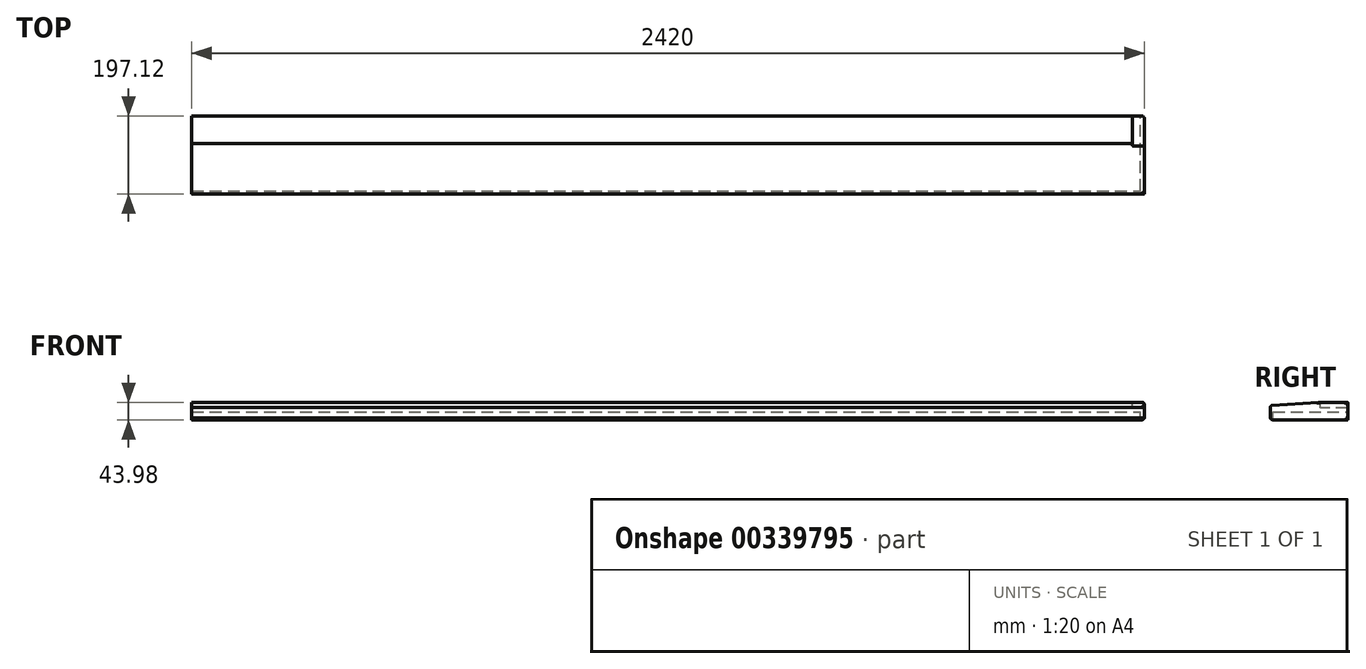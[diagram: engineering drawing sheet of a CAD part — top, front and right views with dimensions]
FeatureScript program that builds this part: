
annotation { "Feature Type Name" : "Feature", "Feature Type Description" : "" }
export const myFeature = defineFeature(function(context is Context, id is Id, definition is map)
    precondition{}
    {
        {
            var Q0;
            Q0=qCreatedBy(makeId("Right.planeOp"),FACE);
            var sketch = newSketch(context, id + "F0", { "sketchPlane" : qUnion([Q0])});
            skLineSegment(sketch, "E0", {"start": v(0, 0) * mm, "end": v(190, 0) * mm});
            skLineSegment(sketch, "E1", {"start": v(-7.12, 10.81) * mm, "end": v(-6.34, -15.77) * mm});
            skLineSegment(sketch, "E2", {"start": v(-1.62, -19.82) * mm, "end": v(0, -19.82) * mm});
            skLineSegment(sketch, "E3", {"start": v(0, -19.82) * mm, "end": v(0, 0) * mm});
            skPoint(sketch, "E4.visualSharp", {"position": v(-8.9, -5.66) * mm});
            skArc(sketch, "E4.filletArc", {"start": v(-6.34, -15.77) * mm, "mid": v(-4.73, -18.67) * mm, "end": v(-1.62, -19.82) * mm});
            skLineSegment(sketch, "E5", {"start": v(114.66, 24.15) * mm, "end": v(-2.47, 16.07) * mm});
            skPoint(sketch, "E6.visualSharp", {"position": v(4.98, 16.59) * mm});
            skArc(sketch, "E6.filletArc", {"start": v(-2.47, 16.07) * mm, "mid": v(-5.87, 14.4) * mm, "end": v(-7.12, 10.81) * mm});
            skLineSegment(sketch, "E7", {"start": v(190, 10) * mm, "end": v(120, 10) * mm});
            skLineSegment(sketch, "E8", {"start": v(190, 0) * mm, "end": v(190, 10) * mm});
            skLineSegment(sketch, "E9", {"start": v(120, 10) * mm, "end": v(120, 19.16) * mm});
            skPoint(sketch, "E10.visualSharp", {"position": v(120, 24.52) * mm});
            skArc(sketch, "E10.filletArc", {"start": v(120, 19.16) * mm, "mid": v(118.41, 22.82) * mm, "end": v(114.66, 24.15) * mm});
            skSolve(sketch);
        }
        {
            var Q0;
            Q0=makeQuery(id+"F0.imprint","IMPRINT",FACE,{"disambiguationData":[TD([[makeQuery(id+"F0.imprint","IMPRINT",EDGE,{"derivedFrom":sQuery(id+"F0.wireOp",EDGE,"E0")}),1.0]])]});
            extrude(context, id + "F1", {"entities" : qUnion([Q0]), "oppositeDirection" : true, "depth" : 2390 * mm});
        }
        {
            var Q0;
            Q0=makeQuery(id+"F1.opExtrude","CAP_FACE",FACE,{"disambiguationData":[OSD([sQuery(id+"F0.wireOp",EDGE,"E0"),sQuery(id+"F0.wireOp",EDGE,"E1"),sQuery(id+"F0.wireOp",EDGE,"E2"),sQuery(id+"F0.wireOp",EDGE,"E3"),sQuery(id+"F0.wireOp",EDGE,"E4.filletArc"),sQuery(id+"F0.wireOp",EDGE,"E5"),sQuery(id+"F0.wireOp",EDGE,"E6.filletArc"),sQuery(id+"F0.wireOp",EDGE,"E7"),sQuery(id+"F0.wireOp",EDGE,"E8"),sQuery(id+"F0.wireOp",EDGE,"E9"),sQuery(id+"F0.wireOp",EDGE,"E10.filletArc")])],"isStart":true});
            var sketch = newSketch(context, id + "F2", { "sketchPlane" : qUnion([Q0])});
            skLineSegment(sketch, "E11.0", {"start": v(-1.62, -19.82) * mm, "end": v(0, -19.82) * mm});
            skArc(sketch, "E11.1", {"start": v(-6.34, -15.77) * mm, "mid": v(-4.73, -18.67) * mm, "end": v(-1.62, -19.82) * mm});
            skLineSegment(sketch, "E11.2", {"start": v(-7.12, 10.81) * mm, "end": v(-6.34, -15.77) * mm});
            skArc(sketch, "E11.3", {"start": v(-2.47, 16.07) * mm, "mid": v(-5.87, 14.4) * mm, "end": v(-7.12, 10.81) * mm});
            skLineSegment(sketch, "E11.4", {"start": v(114.66, 24.15) * mm, "end": v(-2.47, 16.07) * mm});
            skLineSegment(sketch, "E11.5", {"start": v(0, -19.82) * mm, "end": v(0, 0) * mm});
            skLineSegment(sketch, "E11.6", {"start": v(0, 0) * mm, "end": v(190, 0) * mm});
            skLineSegment(sketch, "E11.7", {"start": v(190, 0) * mm, "end": v(190, 10) * mm});
            skLineSegment(sketch, "E12", {"start": v(114.66, 24.15) * mm, "end": v(190, 24.15) * mm});
            skLineSegment(sketch, "E13", {"start": v(190, 24.15) * mm, "end": v(190, 10) * mm});
            skSolve(sketch);
        }
        {
            var Q0;
            Q0=makeQuery(id+"F2.imprint","IMPRINT",FACE,{"disambiguationData":[TD([[makeQuery(id+"F2.imprint","IMPRINT",EDGE,{"derivedFrom":sQuery(id+"F2.wireOp",EDGE,"E11.0")}),1.0]])]});
            var Q1;
            {var subQ1=sQuery(id+"F2.wireOp",EDGE,"E13");Q1=makeQuery(id+"F2.imprint","IMPRINT",FACE,{"disambiguationData":[TD([[makeQuery(id+"F2.imprint","IMPRINT",EDGE,{"derivedFrom":subQ1}),-1.0]])]});}
            extrude(context, id + "F3", {"entities" : qUnion([Q0, Q1]), "operationType" : NewBodyOperationType.ADD, "depth" : 20 * mm});
        }
        {
            var Q0;
            Q0=makeQuery(id+"F3.opExtrude","CAP_FACE",FACE,{"disambiguationData":[OSD([sQuery(id+"F2.wireOp",EDGE,"E11.0"),sQuery(id+"F2.wireOp",EDGE,"E11.1"),sQuery(id+"F2.wireOp",EDGE,"E11.2"),sQuery(id+"F2.wireOp",EDGE,"E11.3"),sQuery(id+"F2.wireOp",EDGE,"E11.4"),sQuery(id+"F2.wireOp",EDGE,"E11.5"),sQuery(id+"F2.wireOp",EDGE,"E11.6"),sQuery(id+"F2.wireOp",EDGE,"E11.7"),sQuery(id+"F2.wireOp",EDGE,"E12"),sQuery(id+"F2.wireOp",EDGE,"E13")])],"isStart":false});
            var sketch = newSketch(context, id + "F4", { "sketchPlane" : qUnion([Q0])});
            skLineSegment(sketch, "E14.0", {"start": v(190, 0) * mm, "end": v(190, 24.15) * mm});
            skLineSegment(sketch, "E14.2", {"start": v(190, 24.15) * mm, "end": v(114.66, 24.15) * mm});
            skLineSegment(sketch, "E14.4", {"start": v(-1.62, -19.82) * mm, "end": v(0, -19.82) * mm});
            skLineSegment(sketch, "E14.5", {"start": v(114.66, 24.15) * mm, "end": v(-2.47, 16.07) * mm});
            skArc(sketch, "E14.6", {"start": v(-2.47, 16.07) * mm, "mid": v(-5.87, 14.4) * mm, "end": v(-7.12, 10.81) * mm});
            skLineSegment(sketch, "E14.7", {"start": v(-7.12, 10.81) * mm, "end": v(-6.34, -15.77) * mm});
            skArc(sketch, "E14.8", {"start": v(-6.34, -15.77) * mm, "mid": v(-4.73, -18.67) * mm, "end": v(-1.62, -19.82) * mm});
            skLineSegment(sketch, "E15", {"start": v(0, -19.82) * mm, "end": v(190, -19.82) * mm});
            skLineSegment(sketch, "E16", {"start": v(190, -19.82) * mm, "end": v(190, 0) * mm});
            skSolve(sketch);
        }
        {
            var Q0;
            Q0 = qSketchRegion(id + "F4", true);
            extrude(context, id + "F5", {"entities" : qUnion([Q0]), "operationType" : NewBodyOperationType.ADD, "depth" : 10 * mm});
        }
        {
            var Q0;
            Q0=makeQuery(id+"F5.opExtrude","CAP_EDGE",EDGE,{"disambiguationData":[OSD([sQuery(id+"F4.wireOp",EDGE,"E14.4"),sQuery(id+"F4.wireOp",EDGE,"E15")])],"isStart":false});
            var Q1;
            Q1=makeQuery(id+"F5.opExtrude","CAP_EDGE",EDGE,{"disambiguationData":[OSD([sQuery(id+"F4.wireOp",EDGE,"E14.5")])],"isStart":false});
            var Q2;
            Q2=makeQuery(id+"F5.opExtrude","CAP_EDGE",EDGE,{"disambiguationData":[OSD([sQuery(id+"F4.wireOp",EDGE,"E14.2")])],"isStart":false});
            var Q3;
            Q3=makeQuery(id+"F5.opExtrude","CAP_EDGE",EDGE,{"disambiguationData":[OSD([sQuery(id+"F4.wireOp",EDGE,"E14.0"),sQuery(id+"F4.wireOp",EDGE,"E16")])],"isStart":false});
            fillet(context, id + "F6", {"entities" : qUnion([Q0, Q1, Q2, Q3]), "radius" : 5 * mm, "tangentPropagation" : true, "allowEdgeOverflow" : false});
        }
    });
